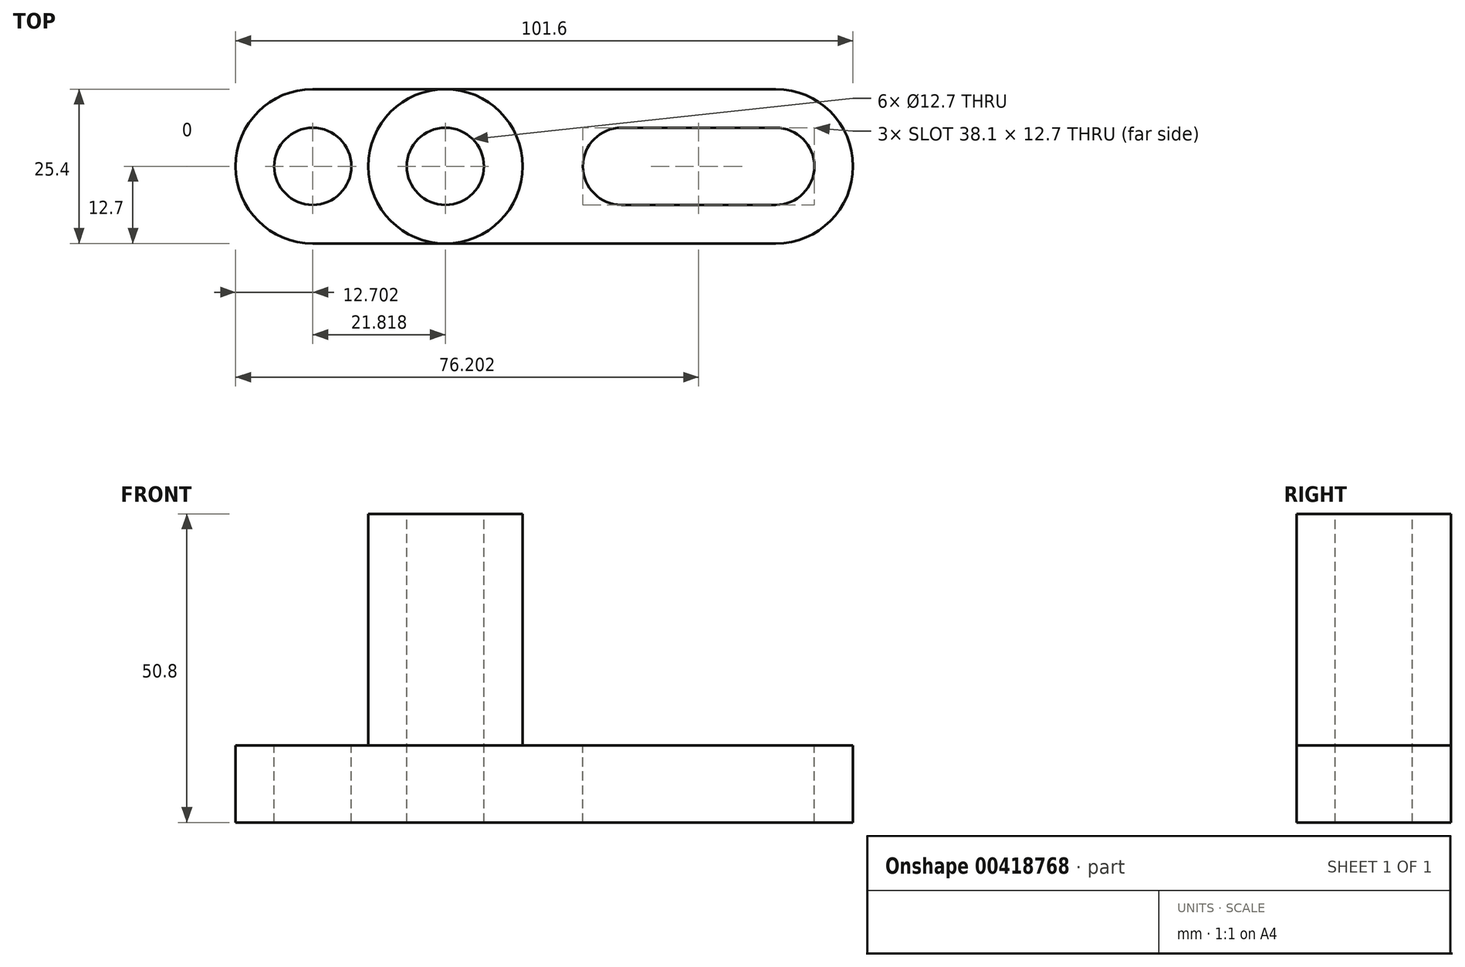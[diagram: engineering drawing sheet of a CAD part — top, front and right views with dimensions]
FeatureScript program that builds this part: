
annotation { "Feature Type Name" : "Feature", "Feature Type Description" : "" }
export const myFeature = defineFeature(function(context is Context, id is Id, definition is map)
    precondition{}
    {
        {
            var Q0;
            Q0=qCreatedBy(makeId("Front.planeOp"),FACE);
            var sketch = newSketch(context, id + "F0", { "sketchPlane" : qUnion([Q0])});
            skLineSegment(sketch, "E0", {"start": v(-21.82, 0) * mm, "end": v(-21.82, 12.7) * mm});
            skLineSegment(sketch, "E1", {"start": v(-21.82, 12.7) * mm, "end": v(0, 12.7) * mm});
            skLineSegment(sketch, "E2", {"start": v(0, 12.7) * mm, "end": v(0, 50.8) * mm});
            skLineSegment(sketch, "E3", {"start": v(0, 50.8) * mm, "end": v(25.4, 50.8) * mm});
            skLineSegment(sketch, "E4", {"start": v(25.4, 50.8) * mm, "end": v(25.4, 12.7) * mm});
            skLineSegment(sketch, "E5", {"start": v(25.4, 12.7) * mm, "end": v(79.78, 12.7) * mm});
            skLineSegment(sketch, "E6", {"start": v(79.78, 12.7) * mm, "end": v(79.78, 0) * mm});
            skLineSegment(sketch, "E7", {"start": v(-21.82, 0) * mm, "end": v(79.78, 0) * mm});
            skSolve(sketch);
        }
        {
            var Q0;
            Q0 = qSketchRegion(id + "F0", true);
            extrude(context, id + "F1", {"entities" : qUnion([Q0]), "depth" : 25.4 * mm});
        }
        {
            var Q0;
            Q0=makeQuery(id+"F1.opExtrude","SWEPT_FACE",FACE,{"disambiguationData":[OSD([sQuery(id+"F0.wireOp",EDGE,"E3")])]});
            var sketch = newSketch(context, id + "F2", { "sketchPlane" : qUnion([Q0])});
            skCircle(sketch, "E8", {"center": v(12.7, -12.7) * mm, "radius": 12.7 * mm});
            skPoint(sketch, "E8.first.point", {"position": v(25.4, -12.7) * mm});
            skPoint(sketch, "E8.second.point", {"position": v(12.7, 0) * mm});
            skPoint(sketch, "E8.third.point", {"position": v(0, -12.7) * mm});
            skCircle(sketch, "E9", {"center": v(12.7, -12.7) * mm, "radius": 6.35 * mm});
            skSolve(sketch);
        }
        {
            var Q0;
            {var subQ0=sQuery(id+"F2.wireOp",EDGE,"E8");var subQ1=sQuery(id+"F0.wireOp",EDGE,"E3");var subQ2=makeQuery(id+"F1.opExtrude","CAP_EDGE",EDGE,{"disambiguationData":[OSD([subQ1])],"isStart":true});var subQ3=makeQuery(id+"F2.imprint","INTERSECT",VERTEX,{"derivedFrom":[subQ2,subQ0]});Q0=makeQuery(id+"F2.imprint","IMPRINT",FACE,{"disambiguationData":[TD([[makeQuery(id+"F2.imprint","IMPRINT",EDGE,{"disambiguationData":[TD([[subQ3,1.0]])],"derivedFrom":subQ0}),-1.0]])]});}
            var Q1;
            {var subQ0=sQuery(id+"F2.wireOp",EDGE,"E8");var subQ1=sQuery(id+"F0.wireOp",EDGE,"E3");var subQ2=makeQuery(id+"F1.opExtrude","CAP_EDGE",EDGE,{"disambiguationData":[OSD([subQ1])],"isStart":true});var subQ3=makeQuery(id+"F2.imprint","INTERSECT",VERTEX,{"derivedFrom":[subQ2,subQ0]});Q1=makeQuery(id+"F2.imprint","IMPRINT",FACE,{"disambiguationData":[TD([[makeQuery(id+"F2.imprint","IMPRINT",EDGE,{"disambiguationData":[TD([[subQ3,-1.0]])],"derivedFrom":subQ0}),-1.0]])]});}
            var Q2;
            {var subQ0=sQuery(id+"F2.wireOp",EDGE,"E8");var subQ1=sQuery(id+"F0.wireOp",EDGE,"E3");var subQ4=makeQuery(id+"F1.opExtrude","CAP_EDGE",EDGE,{"disambiguationData":[OSD([subQ1])],"isStart":false});var subQ5=makeQuery(id+"F2.imprint","INTERSECT",VERTEX,{"derivedFrom":[subQ4,subQ0]});Q2=makeQuery(id+"F2.imprint","IMPRINT",FACE,{"disambiguationData":[TD([[makeQuery(id+"F2.imprint","IMPRINT",EDGE,{"disambiguationData":[TD([[subQ5,1.0]])],"derivedFrom":subQ0}),-1.0]])]});}
            var Q3;
            {var subQ0=sQuery(id+"F2.wireOp",EDGE,"E8");var subQ1=sQuery(id+"F0.wireOp",EDGE,"E3");var subQ4=makeQuery(id+"F1.opExtrude","CAP_EDGE",EDGE,{"disambiguationData":[OSD([subQ1])],"isStart":false});var subQ5=makeQuery(id+"F2.imprint","INTERSECT",VERTEX,{"derivedFrom":[subQ4,subQ0]});Q3=makeQuery(id+"F2.imprint","IMPRINT",FACE,{"disambiguationData":[TD([[makeQuery(id+"F2.imprint","IMPRINT",EDGE,{"disambiguationData":[TD([[subQ5,-1.0]])],"derivedFrom":subQ0}),-1.0]])]});}
            var Q4;
            Q4 = qSketchRegion(id + "F6", true);
            extrude(context, id + "F3", {"entities" : qUnion([Q0, Q1, Q2, Q3, Q4]), "operationType" : NewBodyOperationType.REMOVE, "oppositeDirection" : true, "depth" : 38.1 * mm});
        }
        {
            var Q0;
            {var subQ0=sQuery(id+"F0.wireOp",EDGE,"E3");var subQ1=makeQuery(id+"F1.opExtrude","CAP_EDGE",EDGE,{"disambiguationData":[OSD([subQ0])],"isStart":false});var subQ2=sQuery(id+"F0.wireOp",EDGE,"E2");var subQ3=makeQuery(id+"F1.opExtrude","SWEPT_EDGE",EDGE,{"disambiguationData":[OSD([subQ2,subQ0])]});var subQ4=makeQuery(id+"F2.imprint","INTERSECT",VERTEX,{"derivedFrom":[subQ3,subQ1]});var subQ5=sQuery(id+"F2.wireOp",EDGE,"E8");var subQ6=makeQuery(id+"F2.imprint","INTERSECT",VERTEX,{"derivedFrom":[subQ1,subQ5]});var subQ8=makeQuery(id+"F1.opExtrude","CAP_EDGE",EDGE,{"disambiguationData":[OSD([subQ0])],"isStart":true});var subQ9=makeQuery(id+"F2.imprint","INTERSECT",VERTEX,{"derivedFrom":[subQ3,subQ8]});var subQ10=makeQuery(id+"F2.imprint","INTERSECT",VERTEX,{"derivedFrom":[subQ8,subQ5]});Q0=makeQuery(id+"F3.boolean.opBoolean","MERGE",FACE,{"derivedFrom":[makeQuery(id+"F1.opExtrude","SWEPT_FACE",FACE,{"disambiguationData":[OSD([sQuery(id+"F0.wireOp",EDGE,"E1")])]}),makeQuery(id+"F3.opExtrude","CAP_FACE",FACE,{"disambiguationData":[OSD([subQ2,subQ0,subQ5]),TDD([makeQuery(id+"F2.imprint","IMPRINT",EDGE,{"disambiguationData":[TD([[subQ10,-1.0]])],"derivedFrom":subQ5}),makeQuery(id+"F2.imprint","IMPRINT",EDGE,{"disambiguationData":[TD([[subQ9,1.0]])],"derivedFrom":subQ3}),makeQuery(id+"F2.imprint","IMPRINT",EDGE,{"disambiguationData":[TD([[subQ10,1.0]])],"derivedFrom":subQ8})])],"isStart":false}),makeQuery(id+"F3.opExtrude","CAP_FACE",FACE,{"disambiguationData":[OSD([subQ2,subQ0,subQ5]),TDD([makeQuery(id+"F2.imprint","IMPRINT",EDGE,{"disambiguationData":[TD([[subQ6,1.0]])],"derivedFrom":subQ5}),makeQuery(id+"F2.imprint","IMPRINT",EDGE,{"disambiguationData":[TD([[subQ4,-1.0]])],"derivedFrom":subQ3}),makeQuery(id+"F2.imprint","IMPRINT",EDGE,{"disambiguationData":[TD([[subQ6,1.0]])],"derivedFrom":subQ1})])],"isStart":false})]});}
            var sketch = newSketch(context, id + "F4", { "sketchPlane" : qUnion([Q0])});
            skCircle(sketch, "E10", {"center": v(-9.12, -12.7) * mm, "radius": 6.35 * mm});
            skPoint(sketch, "E10.centerSnap0", {"position": v(-21.82, -12.7) * mm});
            skArc(sketch, "E11", {"start": v(-9.12, 0) * mm, "mid": v(-21.82, -12.7) * mm, "end": v(-9.12, -25.4) * mm});
            skSolve(sketch);
        }
        {
            var Q0;
            Q0 = qSketchRegion(id + "F4", true);
            var Q1;
            {var subQ0=sQuery(id+"F4.wireOp",EDGE,"E11");var subQ3=sQuery(id+"F0.wireOp",EDGE,"E1");var subQ6=makeQuery(id+"F1.opExtrude","SWEPT_EDGE",EDGE,{"disambiguationData":[OSD([sQuery(id+"F0.wireOp",EDGE,"E0"),subQ3])]});var subQ7=makeQuery(id+"F4.imprint","INTERSECT",VERTEX,{"derivedFrom":[subQ6,subQ0]});Q1=makeQuery(id+"F4.imprint","IMPRINT",FACE,{"disambiguationData":[TD([[makeQuery(id+"F4.imprint","IMPRINT",EDGE,{"disambiguationData":[TD([[subQ7,1.0]])],"derivedFrom":subQ0}),-1.0]])]});}
            var Q2;
            {var subQ0=sQuery(id+"F4.wireOp",EDGE,"E11");var subQ3=sQuery(id+"F0.wireOp",EDGE,"E1");var subQ6=makeQuery(id+"F1.opExtrude","SWEPT_EDGE",EDGE,{"disambiguationData":[OSD([sQuery(id+"F0.wireOp",EDGE,"E0"),subQ3])]});var subQ7=makeQuery(id+"F4.imprint","INTERSECT",VERTEX,{"derivedFrom":[subQ6,subQ0]});Q2=makeQuery(id+"F4.imprint","IMPRINT",FACE,{"disambiguationData":[TD([[makeQuery(id+"F4.imprint","IMPRINT",EDGE,{"disambiguationData":[TD([[subQ7,-1.0]])],"derivedFrom":subQ0}),-1.0]])]});}
            extrude(context, id + "F5", {"entities" : qUnion([Q0, Q1, Q2]), "operationType" : NewBodyOperationType.REMOVE, "oppositeDirection" : true, "depth" : 25.4 * mm});
        }
        {
            var Q0;
            {var subQ0=sQuery(id+"F0.wireOp",EDGE,"E3");var subQ1=makeQuery(id+"F1.opExtrude","CAP_EDGE",EDGE,{"disambiguationData":[OSD([subQ0])],"isStart":false});var subQ2=sQuery(id+"F0.wireOp",EDGE,"E4");var subQ3=makeQuery(id+"F1.opExtrude","SWEPT_EDGE",EDGE,{"disambiguationData":[OSD([subQ0,subQ2])]});var subQ4=makeQuery(id+"F2.imprint","INTERSECT",VERTEX,{"derivedFrom":[subQ3,subQ1]});var subQ5=sQuery(id+"F2.wireOp",EDGE,"E8");var subQ6=makeQuery(id+"F2.imprint","INTERSECT",VERTEX,{"derivedFrom":[subQ1,subQ5]});var subQ8=makeQuery(id+"F1.opExtrude","CAP_EDGE",EDGE,{"disambiguationData":[OSD([subQ0])],"isStart":true});var subQ9=makeQuery(id+"F2.imprint","INTERSECT",VERTEX,{"derivedFrom":[subQ3,subQ8]});var subQ10=makeQuery(id+"F2.imprint","INTERSECT",VERTEX,{"derivedFrom":[subQ8,subQ5]});Q0=makeQuery(id+"F3.boolean.opBoolean","MERGE",FACE,{"derivedFrom":[makeQuery(id+"F1.opExtrude","SWEPT_FACE",FACE,{"disambiguationData":[OSD([sQuery(id+"F0.wireOp",EDGE,"E5")])]}),makeQuery(id+"F3.opExtrude","CAP_FACE",FACE,{"disambiguationData":[OSD([subQ0,subQ2,subQ5]),TDD([makeQuery(id+"F2.imprint","IMPRINT",EDGE,{"disambiguationData":[TD([[subQ10,1.0]])],"derivedFrom":subQ5}),makeQuery(id+"F2.imprint","IMPRINT",EDGE,{"disambiguationData":[TD([[subQ9,1.0]])],"derivedFrom":subQ3}),makeQuery(id+"F2.imprint","IMPRINT",EDGE,{"disambiguationData":[TD([[subQ10,-1.0]])],"derivedFrom":subQ8})])],"isStart":false}),makeQuery(id+"F3.opExtrude","CAP_FACE",FACE,{"disambiguationData":[OSD([subQ0,subQ2,subQ5]),TDD([makeQuery(id+"F2.imprint","IMPRINT",EDGE,{"disambiguationData":[TD([[subQ6,-1.0]])],"derivedFrom":subQ5}),makeQuery(id+"F2.imprint","IMPRINT",EDGE,{"disambiguationData":[TD([[subQ4,-1.0]])],"derivedFrom":subQ3}),makeQuery(id+"F2.imprint","IMPRINT",EDGE,{"disambiguationData":[TD([[subQ6,-1.0]])],"derivedFrom":subQ1})])],"isStart":false})]});}
            var sketch = newSketch(context, id + "F6", { "sketchPlane" : qUnion([Q0])});
            skCircle(sketch, "E12", {"center": v(67.08, -12.7) * mm, "radius": 6.35 * mm});
            skCircle(sketch, "E13", {"center": v(41.68, -12.7) * mm, "radius": 6.35 * mm});
            skLineSegment(sketch, "E14", {"start": v(41.68, -19.05) * mm, "end": v(67.08, -19.05) * mm});
            skLineSegment(sketch, "E15", {"start": v(41.68, -6.35) * mm, "end": v(67.08, -6.35) * mm});
            skArc(sketch, "E16", {"start": v(67.08, -25.4) * mm, "mid": v(79.78, -12.7) * mm, "end": v(67.08, 0) * mm});
            skSolve(sketch);
        }
        {
            var Q0;
            {var subQ0=sQuery(id+"F6.wireOp",EDGE,"E16");var subQ3=sQuery(id+"F0.wireOp",EDGE,"E5");var subQ6=makeQuery(id+"F1.opExtrude","SWEPT_EDGE",EDGE,{"disambiguationData":[OSD([subQ3,sQuery(id+"F0.wireOp",EDGE,"E6")])]});var subQ7=makeQuery(id+"F6.imprint","INTERSECT",VERTEX,{"derivedFrom":[subQ6,subQ0]});Q0=makeQuery(id+"F6.imprint","IMPRINT",FACE,{"disambiguationData":[TD([[makeQuery(id+"F6.imprint","IMPRINT",EDGE,{"disambiguationData":[TD([[subQ7,-1.0]])],"derivedFrom":subQ0}),-1.0]])]});}
            var Q1;
            {var subQ0=sQuery(id+"F6.wireOp",EDGE,"E16");var subQ3=sQuery(id+"F0.wireOp",EDGE,"E5");var subQ6=makeQuery(id+"F1.opExtrude","SWEPT_EDGE",EDGE,{"disambiguationData":[OSD([subQ3,sQuery(id+"F0.wireOp",EDGE,"E6")])]});var subQ7=makeQuery(id+"F6.imprint","INTERSECT",VERTEX,{"derivedFrom":[subQ6,subQ0]});Q1=makeQuery(id+"F6.imprint","IMPRINT",FACE,{"disambiguationData":[TD([[makeQuery(id+"F6.imprint","IMPRINT",EDGE,{"disambiguationData":[TD([[subQ7,1.0]])],"derivedFrom":subQ0}),-1.0]])]});}
            var Q2;
            {var subQ0=sQuery(id+"F6.wireOp",EDGE,"E12");var subQ1=makeQuery(id+"F6.imprint","INTERSECT",VERTEX,{"derivedFrom":[subQ0,sQuery(id+"F6.wireOp",EDGE,"E14")]});Q2=makeQuery(id+"F6.imprint","IMPRINT",FACE,{"disambiguationData":[TD([[makeQuery(id+"F6.imprint","IMPRINT",EDGE,{"disambiguationData":[TD([[subQ1,1.0]])],"derivedFrom":subQ0}),1.0]])]});}
            var Q3;
            {var subQ0=sQuery(id+"F6.wireOp",EDGE,"E14");Q3=makeQuery(id+"F6.imprint","IMPRINT",FACE,{"disambiguationData":[TD([[makeQuery(id+"F6.imprint","IMPRINT",EDGE,{"derivedFrom":subQ0}),1.0]])]});}
            var Q4;
            {var subQ0=sQuery(id+"F6.wireOp",EDGE,"E13");var subQ1=makeQuery(id+"F6.imprint","INTERSECT",VERTEX,{"derivedFrom":[subQ0,sQuery(id+"F6.wireOp",EDGE,"E14")]});Q4=makeQuery(id+"F6.imprint","IMPRINT",FACE,{"disambiguationData":[TD([[makeQuery(id+"F6.imprint","IMPRINT",EDGE,{"disambiguationData":[TD([[subQ1,1.0]])],"derivedFrom":subQ0}),1.0]])]});}
            extrude(context, id + "F7", {"entities" : qUnion([Q0, Q1, Q2, Q3, Q4]), "operationType" : NewBodyOperationType.REMOVE, "oppositeDirection" : true, "depth" : 25.4 * mm});
        }
        {
            var Q0;
            Q0=makeQuery(id+"F1.opExtrude","SWEPT_FACE",FACE,{"disambiguationData":[OSD([sQuery(id+"F0.wireOp",EDGE,"E3")])]});
            var sketch = newSketch(context, id + "F8", { "sketchPlane" : qUnion([Q0])});
            skCircle(sketch, "E17", {"center": v(12.7, -12.7) * mm, "radius": 6.35 * mm});
            skSolve(sketch);
        }
        {
            var Q0;
            Q0=makeQuery(id+"F8.imprint","IMPRINT",FACE,{"disambiguationData":[TD([[makeQuery(id+"F8.imprint","IMPRINT",EDGE,{"derivedFrom":sQuery(id+"F8.wireOp",EDGE,"E17")}),1.0]])]});
            extrude(context, id + "F9", {"entities" : qUnion([Q0]), "operationType" : NewBodyOperationType.REMOVE, "oppositeDirection" : true, "depth" : 127 * mm});
        }
    });
